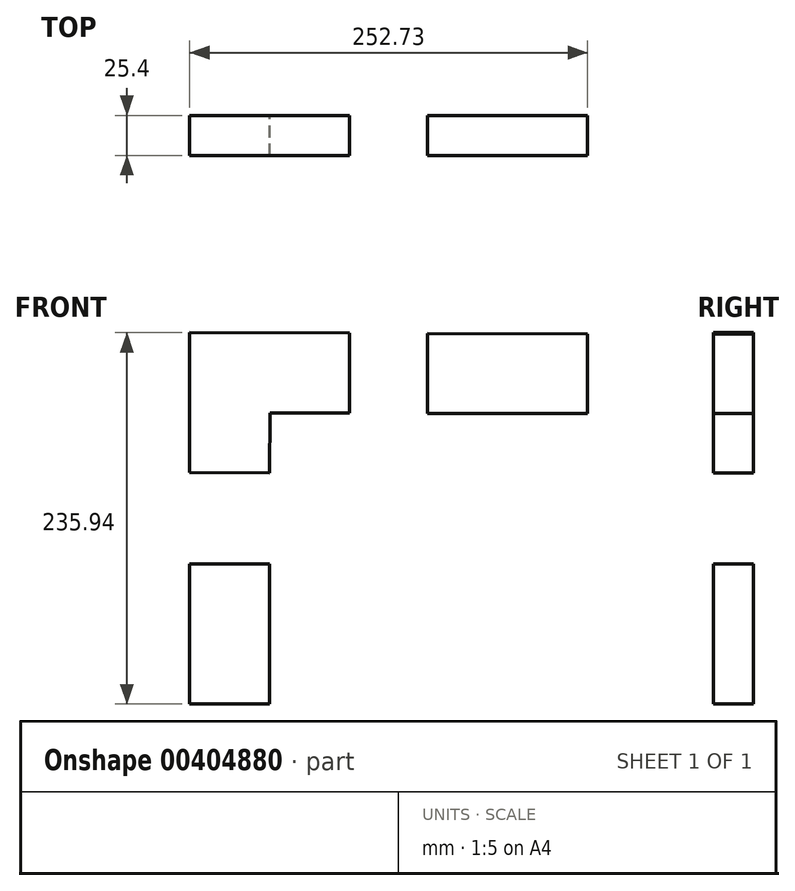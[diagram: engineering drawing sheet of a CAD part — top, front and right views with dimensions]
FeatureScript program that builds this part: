
annotation { "Feature Type Name" : "Feature", "Feature Type Description" : "" }
export const myFeature = defineFeature(function(context is Context, id is Id, definition is map)
    precondition{}
    {
        {
            var Q0;
            Q0=qCreatedBy(makeId("Front.planeOp"),FACE);
            var sketch = newSketch(context, id + "F0", { "sketchPlane" : qUnion([Q0])});
            skLineSegment(sketch, "E0", {"start": v(0, 0) * mm, "end": v(252.73, 0) * mm});
            skLineSegment(sketch, "E1", {"start": v(252.73, 0) * mm, "end": v(252.73, 234.95) * mm});
            skLineSegment(sketch, "E2", {"start": v(0, 235.94) * mm, "end": v(252.73, 234.95) * mm});
            skLineSegment(sketch, "E3", {"start": v(0, 184.74) * mm, "end": v(101.6, 184.74) * mm});
            skLineSegment(sketch, "E4", {"start": v(101.6, 184.74) * mm, "end": v(101.6, 235.54) * mm});
            skLineSegment(sketch, "E5", {"start": v(101.6, 235.54) * mm, "end": v(-79.13, 236.25) * mm});
            skLineSegment(sketch, "E6", {"start": v(252.73, 184.55) * mm, "end": v(151.13, 184.55) * mm});
            skLineSegment(sketch, "E7", {"start": v(151.13, 184.55) * mm, "end": v(151.13, 235.35) * mm});
            skLineSegment(sketch, "E8", {"start": v(50.8, 0) * mm, "end": v(50.8, 88.9) * mm});
            skLineSegment(sketch, "E9", {"start": v(50.8, 88.9) * mm, "end": v(0, 88.9) * mm});
            skLineSegment(sketch, "E10", {"start": v(51.15, 235.74) * mm, "end": v(50.8, 146.84) * mm});
            skLineSegment(sketch, "E11", {"start": v(50.8, 146.84) * mm, "end": v(0, 147.04) * mm});
            skLineSegment(sketch, "E12", {"start": v(0, 235.94) * mm, "end": v(0, 0) * mm});
            skSolve(sketch);
        }
        {
            var Q0;
            {var subQ3=sQuery(id+"F0.wireOp",EDGE,"E6");Q0=makeQuery(id+"F0.imprint","IMPRINT",FACE,{"disambiguationData":[TD([[makeQuery(id+"F0.imprint","IMPRINT",EDGE,{"derivedFrom":subQ3}),-1.0]])]});}
            var Q1;
            {var subQ0=sQuery(id+"F0.wireOp",EDGE,"E4");Q1=makeQuery(id+"F0.imprint","IMPRINT",FACE,{"disambiguationData":[TD([[makeQuery(id+"F0.imprint","IMPRINT",EDGE,{"derivedFrom":subQ0}),1.0]])]});}
            extrude(context, id + "F1", {"entities" : qUnion([Q0, Q1]), "depth" : 25.4 * mm});
        }
        {
            var Q0;
            {var subQ3=sQuery(id+"F0.wireOp",EDGE,"E8");Q0=makeQuery(id+"F0.imprint","IMPRINT",FACE,{"disambiguationData":[TD([[makeQuery(id+"F0.imprint","IMPRINT",EDGE,{"derivedFrom":subQ3}),1.0]])]});}
            extrude(context, id + "F2", {"entities" : qUnion([Q0]), "depth" : 25.4 * mm});
        }
        {
            var Q0;
            {var subQ0=sQuery(id+"F0.wireOp",EDGE,"E12");var subQ1=sQuery(id+"F0.wireOp",EDGE,"E3");var subQ2=makeQuery(id+"F0.imprint","INTERSECT",VERTEX,{"derivedFrom":[subQ1,subQ0]});Q0=makeQuery(id+"F0.imprint","IMPRINT",FACE,{"disambiguationData":[TD([[makeQuery(id+"F0.imprint","IMPRINT",EDGE,{"disambiguationData":[TD([[subQ2,-1.0]])],"derivedFrom":subQ1}),1.0]])]});}
            var Q1;
            {var subQ5=sQuery(id+"F0.wireOp",EDGE,"E11");Q1=makeQuery(id+"F0.imprint","IMPRINT",FACE,{"disambiguationData":[TD([[makeQuery(id+"F0.imprint","IMPRINT",EDGE,{"derivedFrom":subQ5}),-1.0]])]});}
            extrude(context, id + "F3", {"entities" : qUnion([Q0, Q1]), "operationType" : NewBodyOperationType.ADD, "depth" : 25.4 * mm});
        }
        {
            var Q0;
            Q0=sQuery(id+"F0.wireOp",EDGE,"E12");
            extrude(context, id + "F4", {"bodyType" : ToolBodyType.SURFACE, "surfaceEntities" : qUnion([Q0]), "depth" : 50.8 * mm});
        }
        {
            var Q0;
            Q0=sQuery(id+"F0.wireOp",EDGE,"E2");
            extrude(context, id + "F5", {"bodyType" : ToolBodyType.SURFACE, "surfaceEntities" : qUnion([Q0]), "depth" : 50.8 * mm});
        }
        {
            var Q0;
            Q0=sQuery(id+"F0.wireOp",EDGE,"E0");
            extrude(context, id + "F6", {"bodyType" : ToolBodyType.SURFACE, "surfaceEntities" : qUnion([Q0]), "depth" : 50.8 * mm});
        }
        {
            var Q0;
            Q0=sQuery(id+"F0.wireOp",EDGE,"E1");
            extrude(context, id + "F7", {"bodyType" : ToolBodyType.SURFACE, "surfaceEntities" : qUnion([Q0]), "depth" : 50.8 * mm});
        }
    });
